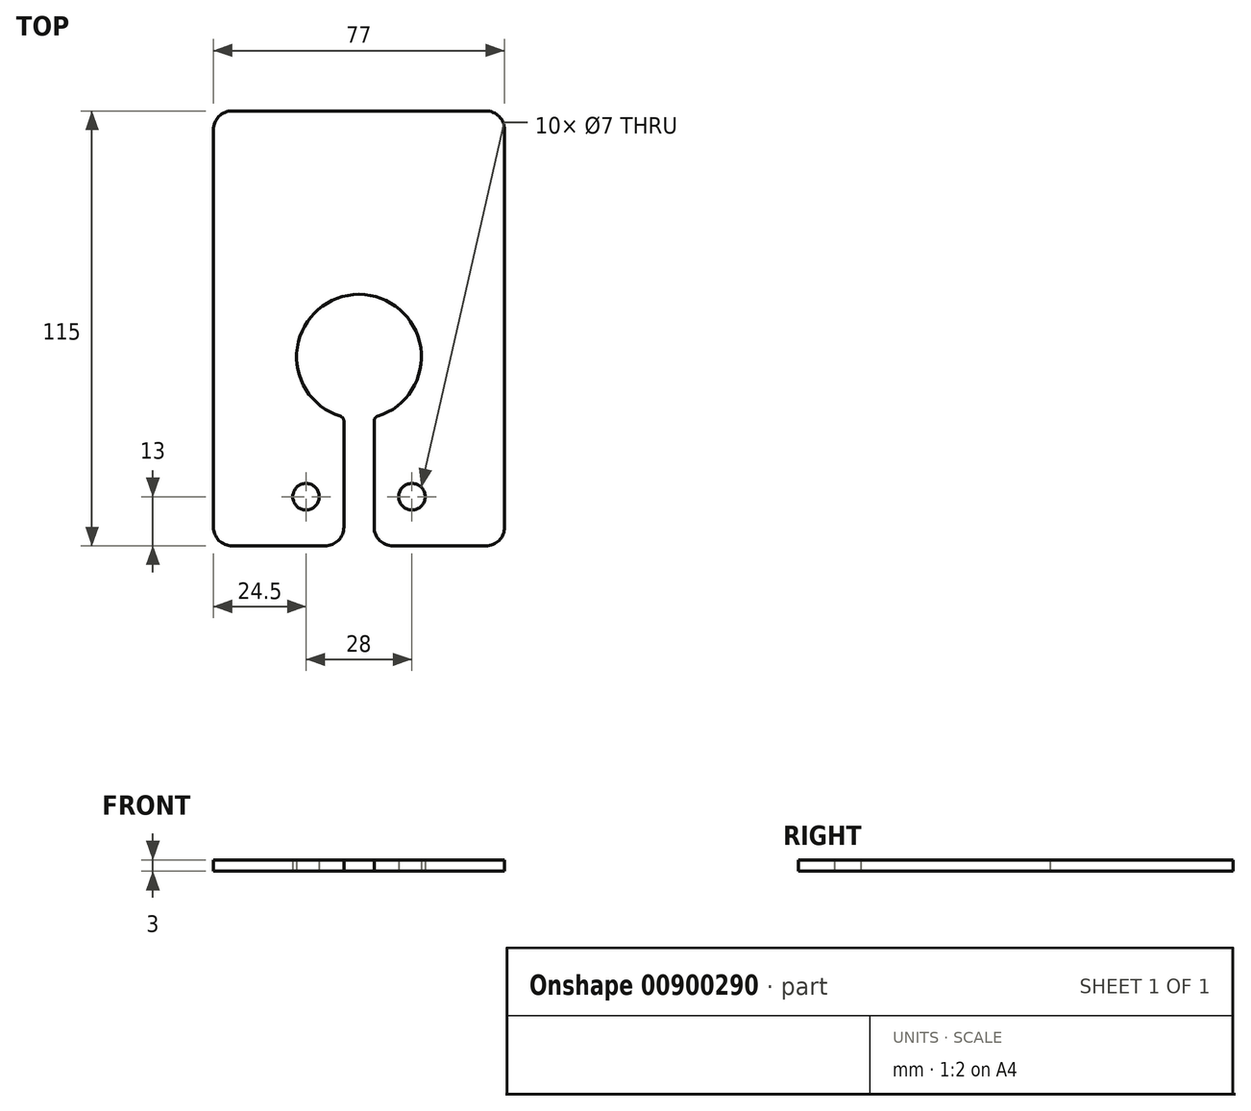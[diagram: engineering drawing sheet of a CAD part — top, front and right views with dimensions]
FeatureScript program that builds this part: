
annotation { "Feature Type Name" : "Feature", "Feature Type Description" : "" }
export const myFeature = defineFeature(function(context is Context, id is Id, definition is map)
    precondition{}
    {
        {
            var Q0;
            Q0=qCreatedBy(makeId("Top.planeOp"),FACE);
            var sketch = newSketch(context, id + "F0", { "sketchPlane" : qUnion([Q0])});
            skLineSegment(sketch, "E0.bottom", {"start": v(38.5, 57.5) * mm, "end": v(-38.5, 57.5) * mm});
            skLineSegment(sketch, "E0.top", {"start": v(38.5, -57.5) * mm, "end": v(4, -57.5) * mm});
            skLineSegment(sketch, "E0.left", {"start": v(38.5, 57.5) * mm, "end": v(38.5, -57.5) * mm});
            skLineSegment(sketch, "E0.right", {"start": v(-38.5, 57.5) * mm, "end": v(-38.5, -57.5) * mm});
            skPoint(sketch, "E0.middle", {"position": v(0, 0) * mm});
            skPoint(sketch, "E1", {"position": v(0, -7.5) * mm});
            skArc(sketch, "E2", {"start": v(4, -23.5) * mm, "mid": v(0, 9) * mm, "end": v(-4, -23.5) * mm});
            skLineSegment(sketch, "E3", {"start": v(-4, -57.5) * mm, "end": v(-4, -23.5) * mm});
            skLineSegment(sketch, "E4", {"start": v(4, -57.5) * mm, "end": v(4, -23.5) * mm});
            skLineSegment(sketch, "E5.trimOffspring", {"start": v(-4, -57.5) * mm, "end": v(-38.5, -57.5) * mm});
            skCircle(sketch, "E6", {"center": v(-14, -44.5) * mm, "radius": 3.5 * mm});
            skCircle(sketch, "E7", {"center": v(14, -44.5) * mm, "radius": 3.5 * mm});
            skSolve(sketch);
        }
        {
            var Q0;
            Q0=makeQuery(id+"F0.imprint","IMPRINT",FACE,{"disambiguationData":[TD([[makeQuery(id+"F0.imprint","IMPRINT",EDGE,{"derivedFrom":sQuery(id+"F0.wireOp",EDGE,"E0.bottom")}),1.0]])]});
            extrude(context, id + "F1", {"entities" : qUnion([Q0]), "depth" : 3 * mm, "offsetDistance" : 25.4 * mm});
        }
        {
            var Q0;
            Q0=makeQuery(id+"F1.opExtrude","SWEPT_EDGE",EDGE,{"disambiguationData":[OSD([sQuery(id+"F0.wireOp",EDGE,"E0.bottom"),sQuery(id+"F0.wireOp",EDGE,"E0.right")])]});
            var Q1;
            Q1=makeQuery(id+"F1.opExtrude","SWEPT_EDGE",EDGE,{"disambiguationData":[OSD([sQuery(id+"F0.wireOp",EDGE,"E0.bottom"),sQuery(id+"F0.wireOp",EDGE,"E0.left")])]});
            var Q2;
            Q2=makeQuery(id+"F1.opExtrude","SWEPT_EDGE",EDGE,{"disambiguationData":[OSD([sQuery(id+"F0.wireOp",EDGE,"E0.right"),sQuery(id+"F0.wireOp",EDGE,"E5.trimOffspring")])]});
            var Q3;
            Q3=makeQuery(id+"F1.opExtrude","SWEPT_EDGE",EDGE,{"disambiguationData":[OSD([sQuery(id+"F0.wireOp",EDGE,"E0.top"),sQuery(id+"F0.wireOp",EDGE,"E0.left")])]});
            var Q4;
            Q4=makeQuery(id+"F1.opExtrude","SWEPT_EDGE",EDGE,{"disambiguationData":[OSD([sQuery(id+"F0.wireOp",EDGE,"E0.top"),sQuery(id+"F0.wireOp",EDGE,"E4")])]});
            var Q5;
            Q5=makeQuery(id+"F1.opExtrude","SWEPT_EDGE",EDGE,{"disambiguationData":[OSD([sQuery(id+"F0.wireOp",EDGE,"E3"),sQuery(id+"F0.wireOp",EDGE,"E5.trimOffspring")])]});
            fillet(context, id + "F2", {"entities" : qUnion([Q0, Q1, Q2, Q3, Q4, Q5]), "radius" : 5 * mm, "tangentPropagation" : true, "allowEdgeOverflow" : false});
        }
        {
            var Q0;
            Q0=makeQuery(id+"F1.opExtrude","SWEPT_EDGE",EDGE,{"disambiguationData":[OSD([sQuery(id+"F0.wireOp",EDGE,"E2"),sQuery(id+"F0.wireOp",EDGE,"E4")])]});
            var Q1;
            Q1=makeQuery(id+"F1.opExtrude","SWEPT_EDGE",EDGE,{"disambiguationData":[OSD([sQuery(id+"F0.wireOp",EDGE,"E2"),sQuery(id+"F0.wireOp",EDGE,"E3")])]});
            fillet(context, id + "F3", {"entities" : qUnion([Q0, Q1]), "radius" : 1.27 * mm, "tangentPropagation" : true, "allowEdgeOverflow" : false});
        }
    });
